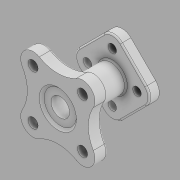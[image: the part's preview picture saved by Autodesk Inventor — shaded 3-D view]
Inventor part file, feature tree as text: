
AUTODESK INVENTOR PART (.ipt)
format: ipt  version: 2020 (Build 240168000, 168)  size: 246,272 bytes
history: native  units: in
note: dims shown in document units (in); Inventor stores cm internally (conversion verified against a paired STEP export)
features: sketch x4, extrude x3, hole x1, other x1, fillet x1
ambient origin geometry x8: Origin, YZ Plane, XZ Plane, XY Plane, X Axis, Y Axis, Z Axis, Center Point
bodies: Body1 (feature_tree)
feature tree (10):
  extrude  "Base"  Depth=1.0in
  extrude  "Cilindro"  Depth=1.0in
  extrude  "Extrusión5"  Depth=0.5in
  hole  "Agujero1"  [1 undecoded]
  other  "Cara para el ángulo de desmoldeo1"
  fillet  "Empalme1"  Radius=0.344in
  sketch  "Boceto3"  dims[d30=1.0in d31=2.0in]
  sketch  "Boceto4"  dims[d32=2.0in d33=1.0in]
  sketch  "Boceto5"  dims[d34=0.5in d35=0.5in]
  sketch  "Boceto6"  dims[d36=0.5in d37=0.5in d38=0.344in d39=0.344in d40=0.344in d41=0.344in d42=0.4in d43=0.0in d44=1.1in d45=2.2in d46=0.0in d47=2.0in d48=2.0in d49=1.0in d50=1.0in d51=1.0in d52=1.0in d53=0.406in d54=0.406in d55=0.406in d56=0.406in d57=1.0in d58=3.0in d59=3.0in d60=3.0in d61=3.0in d62=0.5in d63=0.0in d64=0.75in d65=0.3511in d66=1.5in d67=0.1in d68=45.0deg d69=1.5in d70=0.0in d71=45.0deg d72=0.06in d14=0.5in d15=0.0344in d16=0.5in d17=0.0344in]
note: 1 required parameter value undecoded (feature->parameter linkage not recoverable at this tier; creation-order binding heuristic only, values carry confidence <= 0.55)
